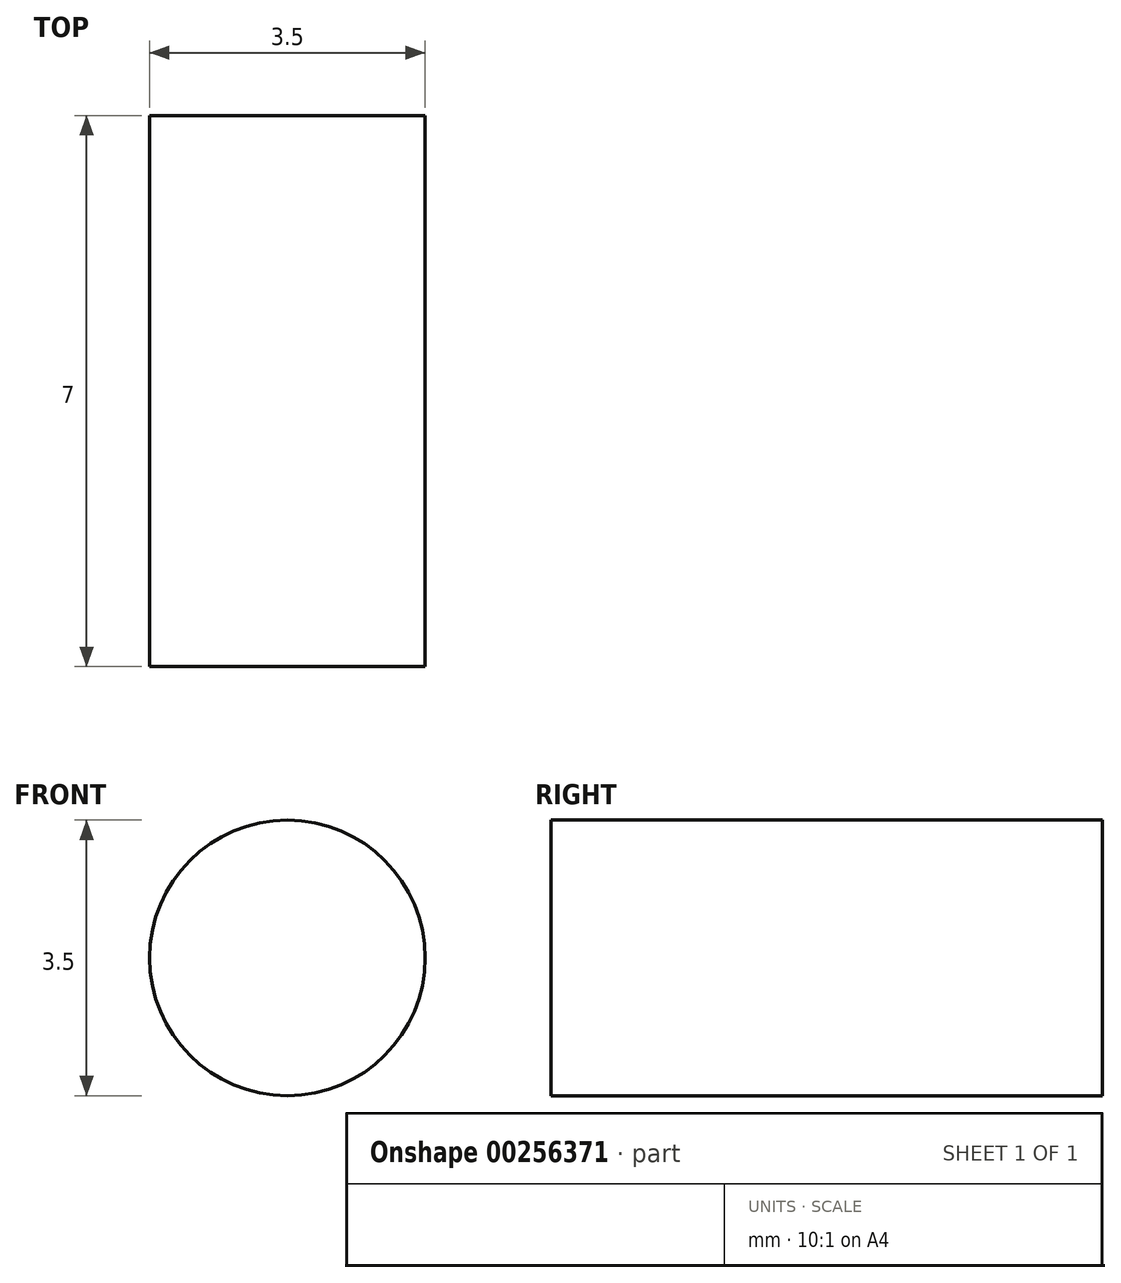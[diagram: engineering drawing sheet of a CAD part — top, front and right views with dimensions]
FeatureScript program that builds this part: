
annotation { "Feature Type Name" : "Feature", "Feature Type Description" : "" }
export const myFeature = defineFeature(function(context is Context, id is Id, definition is map)
    precondition{}
    {
        {
            var Q0;
            Q0=qCreatedBy(makeId("Front.planeOp"),FACE);
            var sketch = newSketch(context, id + "F0", { "sketchPlane" : qUnion([Q0])});
            skCircle(sketch, "E0", {"center": v(0, 0) * mm, "radius": 1.75 * mm});
            skSolve(sketch);
        }
        {
            var Q0;
            Q0 = qSketchRegion(id + "F0", true);
            extrude(context, id + "F1", {"entities" : qUnion([Q0]), "depth" : 7 * mm});
        }
    });
